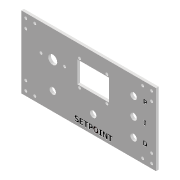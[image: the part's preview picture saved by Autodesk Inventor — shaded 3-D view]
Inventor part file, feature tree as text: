
AUTODESK INVENTOR PART (.ipt)
format: ipt  version: 2022 (Build 260153000, 153)  size: 549,376 bytes
history: native  units: mm
features: sketch x6, extrude x5, projected_geometry x4, other x2
ambient origin geometry x8: Origin, YZ Plane, XZ Plane, XY Plane, X Axis, Y Axis, Z Axis, Center Point
bodies: Body1 (feature_tree)
feature tree (17):
  other  "Sólido1"
  extrude  "Extrusión1"  Depth=80.0mm
  extrude  "Extrusión2"  Depth=3.0mm
  extrude  "Extrusión3"  Depth=7.2mm
  extrude  "Extrusión4"  Depth=20.0mm
  other  "Repujado1"
  extrude  "Extrusión5"  Depth=25.0mm
  sketch  "Boceto1"  dims[d0=150.0mm d1=80.0mm]
  sketch  "Boceto2"  dims[d2=3.0mm d3=0.0mm d4=7.2mm]
  projected_geometry  "Contorno proyectado1"
  sketch  "Boceto3"  dims[d5=7.2mm d6=7.2mm]
  projected_geometry  "Contorno proyectado2"
  sketch  "Boceto4"  dims[d7=20.0mm d8=20.0mm]
  sketch  "Boceto5"  dims[d9=20.0mm d10=25.0mm]
  projected_geometry  "Contorno proyectado3"
  sketch  "Boceto6"  dims[d13=7.2mm d14=45.0mm d15=7.2mm d16=35.0mm d17=35.0mm d18=24.0mm d19=17.5mm d20=40.0mm d21=10.0mm d22=10.0mm d23=10.0mm d24=0.0mm d25=3.2mm d26=3.2mm d27=3.2mm d28=3.2mm d29=30.45mm d32=15.225mm d33=10.0mm d34=0.0mm d35=3.2mm d36=3.2mm d37=26.2mm d38=13.1mm d39=0.0mm d40=0.0mm d41=28.4mm d42=14.2mm d43=0.0mm d44=6.0mm d45=0.5mm d46=0.0mm d47=5.0mm d48=5.0mm d49=5.0mm d50=5.0mm d51=10.0mm d52=10.0mm d53=10.0mm d54=10.0mm d55=3.2mm d56=3.2mm d57=3.2mm d58=3.2mm d59=3.2mm d60=3.2mm d61=3.2mm d62=3.2mm d63=3.2mm d64=3.2mm d65=3.2mm d66=3.2mm d67=0.0mm d68=0.0mm d69=0.5mm d70=0.872665mm]
  projected_geometry  "Contorno proyectado4"
